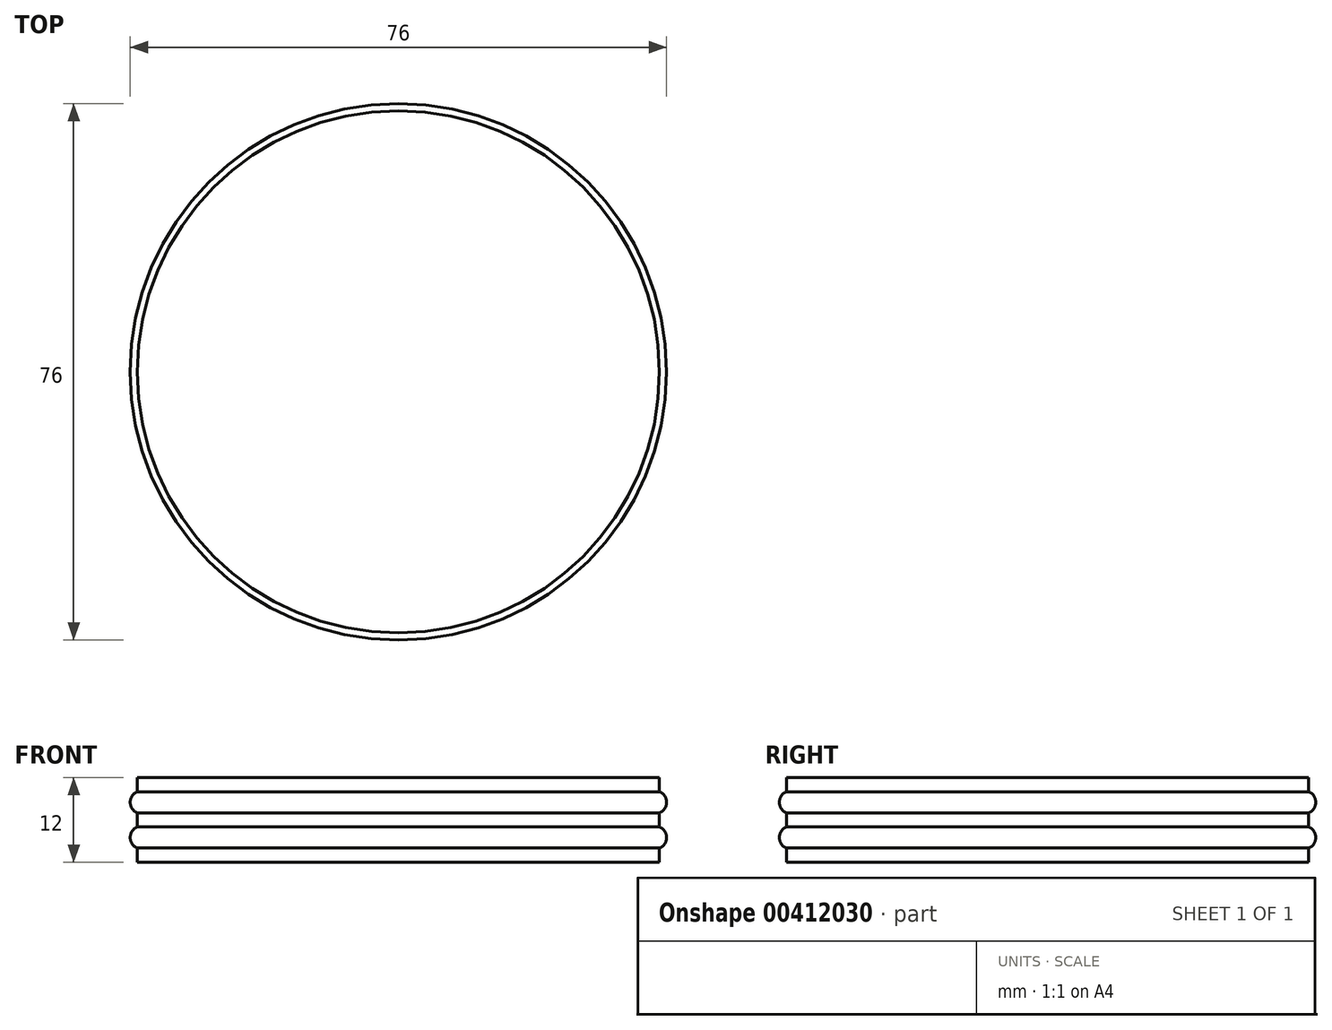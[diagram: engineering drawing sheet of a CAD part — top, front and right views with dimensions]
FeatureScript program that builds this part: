
annotation { "Feature Type Name" : "Feature", "Feature Type Description" : "" }
export const myFeature = defineFeature(function(context is Context, id is Id, definition is map)
    precondition{}
    {
        {
            var Q0;
            Q0=qCreatedBy(makeId("Top.planeOp"),FACE);
            var sketch = newSketch(context, id + "F0", { "sketchPlane" : qUnion([Q0])});
            skCircle(sketch, "E0", {"center": v(0, 0) * mm, "radius": 37 * mm});
            skSolve(sketch);
        }
        {
            var Q0;
            Q0 = qSketchRegion(id + "F0", true);
            extrude(context, id + "F1", {"entities" : qUnion([Q0]), "depth" : 2 * mm});
        }
        {
            var Q0;
            Q0=makeQuery(id+"F1.opExtrude","CAP_FACE",FACE,{"disambiguationData":[OSD([sQuery(id+"F0.wireOp",EDGE,"E0")])],"isStart":false});
            var sketch = newSketch(context, id + "F2", { "sketchPlane" : qUnion([Q0])});
            skCircle(sketch, "E1", {"center": v(0, 0) * mm, "radius": 38 * mm});
            skSolve(sketch);
        }
        {
            var Q0;
            Q0 = qSketchRegion(id + "F2", true);
            extrude(context, id + "F3", {"entities" : qUnion([Q0]), "operationType" : NewBodyOperationType.ADD, "depth" : 3 * mm});
        }
        {
            var Q0;
            Q0=makeQuery(id+"F3.opExtrude","CAP_FACE",FACE,{"disambiguationData":[OSD([sQuery(id+"F2.wireOp",EDGE,"E1")])],"isStart":false});
            var sketch = newSketch(context, id + "F4", { "sketchPlane" : qUnion([Q0])});
            skCircle(sketch, "E2", {"center": v(0, 0) * mm, "radius": 37 * mm});
            skSolve(sketch);
        }
        {
            var Q0;
            Q0 = qSketchRegion(id + "F4", true);
            extrude(context, id + "F5", {"entities" : qUnion([Q0]), "operationType" : NewBodyOperationType.ADD, "depth" : 2 * mm});
        }
        {
            var Q0;
            Q0=makeQuery(id+"F5.opExtrude","CAP_FACE",FACE,{"disambiguationData":[OSD([sQuery(id+"F4.wireOp",EDGE,"E2")])],"isStart":false});
            var sketch = newSketch(context, id + "F6", { "sketchPlane" : qUnion([Q0])});
            skCircle(sketch, "E3", {"center": v(0, 0) * mm, "radius": 38 * mm});
            skSolve(sketch);
        }
        {
            var Q0;
            Q0 = qSketchRegion(id + "F6", true);
            extrude(context, id + "F7", {"entities" : qUnion([Q0]), "operationType" : NewBodyOperationType.ADD, "depth" : 3 * mm});
        }
        {
            var Q0;
            Q0=makeQuery(id+"F7.opExtrude","CAP_FACE",FACE,{"disambiguationData":[OSD([sQuery(id+"F6.wireOp",EDGE,"E3")])],"isStart":false});
            var sketch = newSketch(context, id + "F8", { "sketchPlane" : qUnion([Q0])});
            skCircle(sketch, "E4", {"center": v(0, 0) * mm, "radius": 37 * mm});
            skSolve(sketch);
        }
        {
            var Q0;
            Q0 = qSketchRegion(id + "F8", true);
            extrude(context, id + "F9", {"entities" : qUnion([Q0]), "operationType" : NewBodyOperationType.ADD, "depth" : 2 * mm});
        }
        {
            var Q0;
            Q0=makeQuery(id+"F7.opExtrude","CAP_EDGE",EDGE,{"disambiguationData":[OSD([sQuery(id+"F6.wireOp",EDGE,"E3")])],"isStart":true});
            var Q1;
            Q1=makeQuery(id+"F3.opExtrude","CAP_EDGE",EDGE,{"disambiguationData":[OSD([sQuery(id+"F2.wireOp",EDGE,"E1")])],"isStart":true});
            var Q2;
            Q2=makeQuery(id+"F7.opExtrude","CAP_EDGE",EDGE,{"disambiguationData":[OSD([sQuery(id+"F6.wireOp",EDGE,"E3")])],"isStart":false});
            var Q3;
            Q3=makeQuery(id+"F3.opExtrude","CAP_EDGE",EDGE,{"disambiguationData":[OSD([sQuery(id+"F2.wireOp",EDGE,"E1")])],"isStart":false});
            fillet(context, id + "F10", {"entities" : qUnion([Q0, Q1, Q2, Q3]), "radius" : 1.6 * mm, "tangentPropagation" : true, "allowEdgeOverflow" : false});
        }
    });
